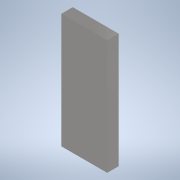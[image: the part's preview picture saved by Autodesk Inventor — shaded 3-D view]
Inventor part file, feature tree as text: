
AUTODESK INVENTOR PART (.ipt)
format: ipt  version: 2022 (Build 260153000, 153)  size: 92,672 bytes
history: native  units: in
note: dims shown in document units (in); Inventor stores cm internally (conversion verified against a paired STEP export)
features: extrude x1, sketch x1
ambient origin geometry x8: Origin, YZ Plane, XZ Plane, XY Plane, X Axis, Y Axis, Z Axis, Center Point
bodies: Solid1 (feature_tree)
feature tree (2):
  extrude  "Extrusion1"  Depth=0.5906in
  sketch  "Sketch1"  dims[d0=0.2362in d1=0.5906in d2=0.0591in d3=0.0in]
